# Revit family: BIMLIB_Муфта_переходная_PEX_РОСТерм
name_source: partatom
category: Соединительные детали трубопроводов
revit_build: Autodesk Revit 2017 (Build: 20170118_1100(x64)
units: mm (PartAtom-declared; Revit-internal decimal feet)

## family parameters
Всегда вертикально = Да
На основе рабочей плоскости = Нет
Общий = Нет
При загрузке вырезать с полостями = Нет
Размер круглого соединителя = Использовать диаметр
Тип детали = Тройник

## types (4) — shared parameters
ADSK_URL документации изделия = http://rostherm.ru
ADSK_URL страницы изделия = http://rostherm.ru
ADSK_Версия Revit = 2017
ADSK_Единица измерения = шт
ADSK_Завод-изготовитель = РОСТерм
BL_BIM library = https://bimlib.pro
URL = http://rostherm.ru
Изготовитель = РОСТерм

## per-type parameters (varying)
| type | ADSK_Марка | ADSK_Материал | Описание |
| BIMLIB_Муфта_переходная_РОСТерм |  | BIMLIB_Черный_РT | Тройник переходной. |
| Муфта переходная | M40-20 | BIMLIB_Белый_РТ | Муфта переходная |
| BIMLIB_Муфта_переходная_PEX_РОСТерм |  | BIMLIB_Черный_РT | Тройник переходной. |
| Муфта переходная PEX |  | BIMLIB_Черный_РT | Муфта переходная |
